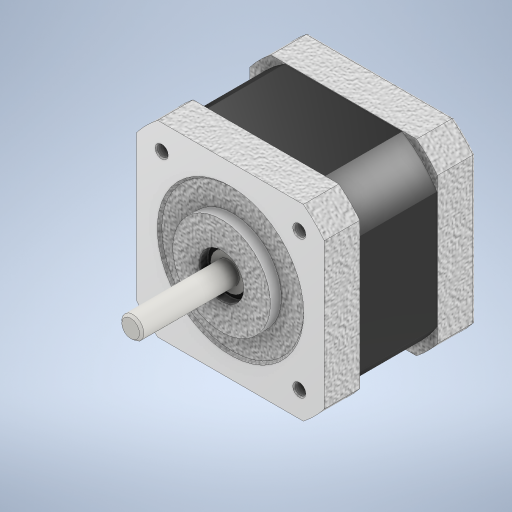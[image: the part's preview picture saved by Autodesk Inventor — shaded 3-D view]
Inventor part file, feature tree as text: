
AUTODESK INVENTOR PART (.ipt)
format: ipt  version: 2024 (Build 280153000, 153)  size: 587,264 bytes
history: native  units: mm
features: extrude x13, projected_geometry x6, chamfer x4, fillet x3, hole x2, plane x2, pattern_circular x2
ambient origin geometry x8: Origin, YZ Plane, XZ Plane, XY Plane, X Axis, Y Axis, Z Axis, Center Point
bodies: Solid1 (feature_tree)
feature tree (32):
  extrude  "Extrusion1"  Depth=42.3mm
  extrude  "Extrusion2"  Depth=42.3mm
  hole  "Hole1"  [1 undecoded]
  plane  "Work Plane1"
  extrude  "Extrusion3"  Depth=31.0mm
  extrude  "Extrusion5"  Depth=49.9mm
  chamfer  "Chamfer1"  Distance=22.0mm
  hole  "Hole2"  [1 undecoded]
  plane  "Work Plane2"
  extrude  "Extrusion6"  Depth=2.0mm TaperAngle=0.0deg
  chamfer  "Chamfer2"  [1 undecoded]
  extrude  "Extrusion7"  Depth=8.5mm TaperAngle=0.0deg
  extrude  "Extrusion8"  Depth=49.85mm
  extrude  "Extrusion9"  Depth=0.1mm
  extrude  "Extrusion10"  Depth=10.0mm TaperAngle=0.0deg
  extrude  "Extrusion11"  Depth=0.25mm TaperAngle=45.0deg
  chamfer  "Chamfer3"  Distance=5.0mm
  extrude  "Extrusion13"  Depth=8.0mm
  pattern_circular  "Circular Pattern1"  [2 undecoded]
  fillet  "Fillet2"  Radius=4.5mm
  fillet  "Fillet3"  Radius=0.5mm
  extrude  "Extrusion12"  Depth=22.298mm TaperAngle=0.0deg
  fillet  "Fillet1"  Radius=0.5mm
  pattern_circular  "Circular Pattern2"  [2 undecoded]
  extrude  "Extrusion14"  Depth=3.0mm TaperAngle=0.0deg
  chamfer  "Chamfer4"  Distance=8.0mm
  projected_geometry  "Projected Loop1"
  projected_geometry  "Projected Loop2"
  projected_geometry  "Projected Loop3"
  projected_geometry  "Projected Loop5"
  projected_geometry  "Projected Loop6"
  projected_geometry  "Projected Loop7"
note: 7 required parameter values undecoded (feature->parameter linkage not recoverable at this tier; creation-order binding heuristic only, values carry confidence <= 0.55)
